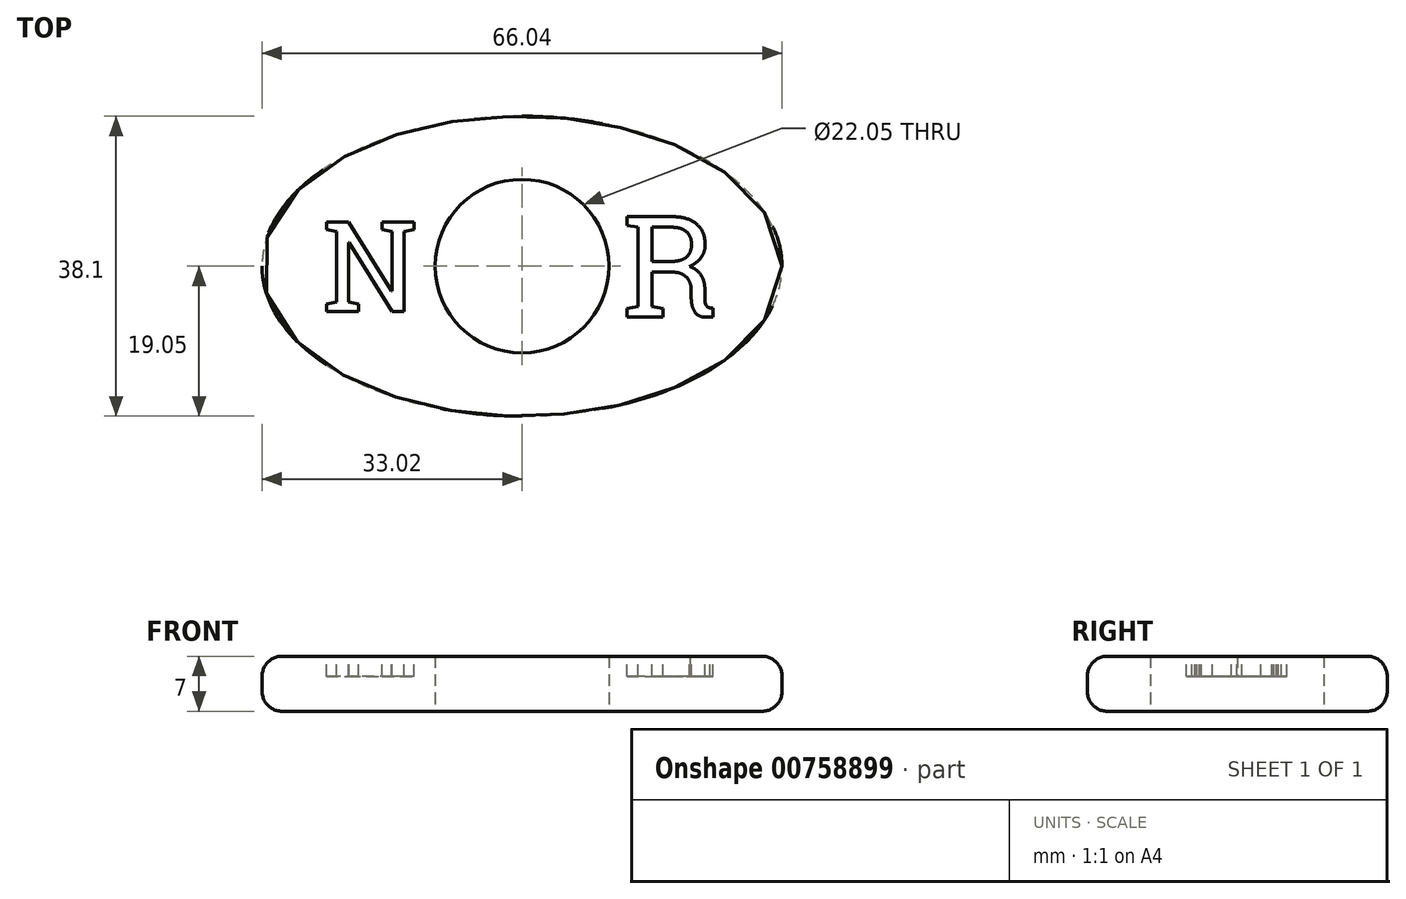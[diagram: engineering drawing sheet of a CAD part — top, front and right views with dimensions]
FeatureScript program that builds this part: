
annotation { "Feature Type Name" : "Feature", "Feature Type Description" : "" }
export const myFeature = defineFeature(function(context is Context, id is Id, definition is map)
    precondition{}
    {
        {
            var Q0;
            Q0=qCreatedBy(makeId("Top.planeOp"),FACE);
            var sketch = newSketch(context, id + "F0", { "sketchPlane" : qUnion([Q0])});
            skEllipse(sketch, "E0", {"center": v(0, 0) * mm, "majorRadius": 33.02 * mm, "minorRadius": 19.05 * mm, "majorAxis": v(1, 0)});
            skCircle(sketch, "E1", {"center": v(0, 0) * mm, "radius": 11.03 * mm});
            skLineSegment(sketch, "E2", {"start": v(-33.02, 0) * mm, "end": v(33.02, 0) * mm, "construction": true});
            skLineSegment(sketch, "E3", {"start": v(0, 19.05) * mm, "end": v(0, -19.05) * mm, "construction": true});
            skSolve(sketch);
        }
        {
            var Q0;
            Q0=makeQuery(id+"F0.imprint","IMPRINT",FACE,{"disambiguationData":[TD([[makeQuery(id+"F0.imprint","IMPRINT",EDGE,{"derivedFrom":sQuery(id+"F0.wireOp",EDGE,"E0")}),1.0]])]});
            extrude(context, id + "F1", {"entities" : qUnion([Q0]), "depth" : 7 * mm, "offsetDistance" : 25.4 * mm});
        }
        {
            var Q0;
            Q0=makeQuery(id+"F1.opExtrude","CAP_EDGE",EDGE,{"disambiguationData":[OSD([sQuery(id+"F0.wireOp",EDGE,"E0")])],"isStart":false});
            var Q1;
            Q1=makeQuery(id+"F1.opExtrude","CAP_EDGE",EDGE,{"disambiguationData":[OSD([sQuery(id+"F0.wireOp",EDGE,"E0")])],"isStart":true});
            fillet(context, id + "F2", {"entities" : qUnion([Q0, Q1]), "radius" : 2.54 * mm, "tangentPropagation" : true, "allowEdgeOverflow" : false});
        }
        {
            var Q0;
            Q0=makeQuery(id+"F1.opExtrude","CAP_FACE",FACE,{"disambiguationData":[OSD([sQuery(id+"F0.wireOp",EDGE,"E0"),sQuery(id+"F0.wireOp",EDGE,"E1")])],"isStart":false});
            var sketch = newSketch(context, id + "F3", { "sketchPlane" : qUnion([Q0])});
            skSolve(sketch);
        }
        {
            var Q0;
            {var subQ0=sQuery(id+"F0.wireOp",EDGE,"E1");Q0=makeQuery(id+"F3.imprint","IMPRINT",FACE,{"disambiguationData":[TD([[makeQuery(id+"F3.imprint","IMPRINT",EDGE,{"derivedFrom":makeQuery(id+"F1.opExtrude","CAP_EDGE",EDGE,{"disambiguationData":[OSD([subQ0])],"isStart":false})}),-1.0]])]});}
            var sketch = newSketch(context, id + "F4", { "sketchPlane" : qUnion([Q0])});
            skText(sketch, "E4", { "text": "N", "fontName": "RobotoSlab-Regular.ttf"});
            skText(sketch, "E5", { "text": "R", "fontName": "RobotoSlab-Regular.ttf"});
            skLineSegment(sketch, "E6", {"start": v(0, 0) * mm, "end": v(-25.4, 0) * mm, "construction": true});
            skLineSegment(sketch, "E7", {"start": v(0, 0) * mm, "end": v(25.4, 0) * mm, "construction": true});
            skLineSegment(sketch, "E8", {"start": v(-25.4, 0) * mm, "end": v(-12.7, 0) * mm, "construction": true});
            skLineSegment(sketch, "E9", {"start": v(12.7, 0) * mm, "end": v(25.4, 0) * mm});
            skPoint(sketch, "E10", {"position": v(19.05, 0) * mm});
            skLineSegment(sketch, "E11", {"start": v(12.7, 0) * mm, "end": v(25.4, 0) * mm, "construction": true});
            skPoint(sketch, "E12", {"position": v(-19.05, 0) * mm});
            const initialGuessF4  = {"E4": [-0.0254, -0.00577, 1, 0, 0.01153], "E5": [0.0127, -0.00648, 1, 0, 0.01295]};
            skSetInitialGuess(sketch, initialGuessF4);
            skSolve(sketch);
        }
        {
            var Q0;
            Q0=qSketchRegion(id+"F4",true);
            extrude(context, id + "F5", {"entities" : qUnion([Q0]), "operationType" : NewBodyOperationType.REMOVE, "oppositeDirection" : true, "depth" : 2.54 * mm, "offsetDistance" : 25.4 * mm});
        }
    });
